# Revit family: 0041775
name_source: partatom
category: Lighting Fixtures
revit_build: Autodesk Revit 2017 (Build: 20160225_1515(x64)
units: mm (PartAtom-declared; Revit-internal decimal feet)

## family parameters
Cut with Voids When Loaded = No
Host = Face
Light Source = Yes
OmniClass Number = 23.80.70.00
OmniClass Title = Lighting
Part Type = Normal
Room Calculation Point = No
Round Connector Dimension = Use Diameter
Shared = No

## types (1)
- 0041775 SYLSAFE XSPOT OA R EM3 NM MS
    Apparent Load = 3 VA
    Assembly Code = D5020200
    AssetType = Fixed
    Chamfer_SYL = 1 mm  [stored 0.00328084 ft]
    ClassificationName = Uniclass2015
    ClassificationValue = EF_70_80
    Color Filter = 16777215
    Cost = 0 $
    Default Elevation = 1219 mm
    Description = SylSafe XSpot OA R EM3 NM MS is a miniature emergency recessed spotlight with small form factor - cut-out diameter: 10mm. Non-maintained 3 hr emergency duration with NiMH rechargeable battery. Recharge period 24 hours. Quick and easy installation with driver module and battery pack contained in articulated case that can placed near the luminaire. Suitable for sheet metal installation. 80lm, 2.8W, IK03, IP20. Power Factor 0.45. Class II electrical construction.
    Dimming Lamp Color Temperature Shift = <None>
    DocumentationLiterature = http://www.sylvania-lighting.com
    ElectricShockClassification = Class II
    Emit from Line Length = 610 mm
    FixingEnd_SYL = -30 mm  [stored -0.0984252 ft]
    FixingStart_SYL = -15 mm  [stored -0.0492126 ft]
    FixingThickness_SYL = 7 mm  [stored 0.0229659 ft]
    FixingThread_SYL = 4 mm  [stored 0.0131234 ft]
    FrameH_SYL = 10 mm  [stored 0.0328084 ft]
    FrameThickness_SYL = 1 mm  [stored 0.00328084 ft]
    FrameWidth_SYL = 9 mm  [stored 0.0295276 ft]
    IfcExportAs = IfcLightFixtureType
    IfcExportType = IfcLightFixtureType
    ImpactProtectionIndex = IK03
    IngressProtection = IP20
    Keynote = 16500
    Lamp = LED
    LampColourRenderingIndex = 70
    LampColourTemperature = 5700 K
    LampH_SYL = 1 mm  [stored 0.00328084 ft]
    LampNominalLuminous = 80 lm
    LampW1_SYL = 5 mm  [stored 0.0164042 ft]
    LampW_SYL = 4 mm  [stored 0.0131234 ft]
    LampsType = LED
    LuminousEfficacy = 29 lm/W
    Manufacturer = Feilo Sylvania
    ManufacturerName = Feilo Sylvania
    Material_1_SYL = Lighting_SYL
    Material_2_SYL = Lighting_SYL
    Material_3_SYL = Lighting_SYL
    Material_4_SYL = LEDLamp_SYL
    Model = SylSafe XSpot OA R EM3 NM MS
    ModelNumber = 0041775
    ModelReference = SylSafe XSpot OA R EM3 NM MS
    Name = SylSafe XSpot OA R EM3 NM MS
    NominalDepth = 12 mm  [stored 0.0393701 ft]
    NominalHeight = 27 mm
    NominalLength = 12 mm  [stored 0.0393701 ft]
    OverTheWall2_SYL = 20 mm  [stored 0.0656168 ft]
    OverTheWall_SYL = 2 mm  [stored 0.00656168 ft]
    Photometric Web File = 0041775.ies
    PowerConsumption = 2.8 W
    PowerFactor = 0.45
    R1_SYL = 5 mm  [stored 0.0164042 ft]
    R_SYL = 6 mm  [stored 0.019685 ft]
    Thread_SYL = 4 mm  [stored 0.0131234 ft]
    Tilt Angle = -90.00°
    Type Image = <None>
    TypeName = SylSafe XSpot OA R EM3 NM MS
    URL = http://www.sylvania-lighting.com
    UnderTheWall1_SYL = 5 mm  [stored 0.0164042 ft]
    Voltage = 0 V
    WallThickness_SYL = 5 mm  [stored 0.0164042 ft]
    Weight = 8.0 kg

note: [stored X ft] marks values corroborated as IEEE doubles in the binary element streams (Revit-internal decimal feet)

## geometry (parser evidence)
native form markers: Sweep x1
no freeform markers — native parametric forms only
